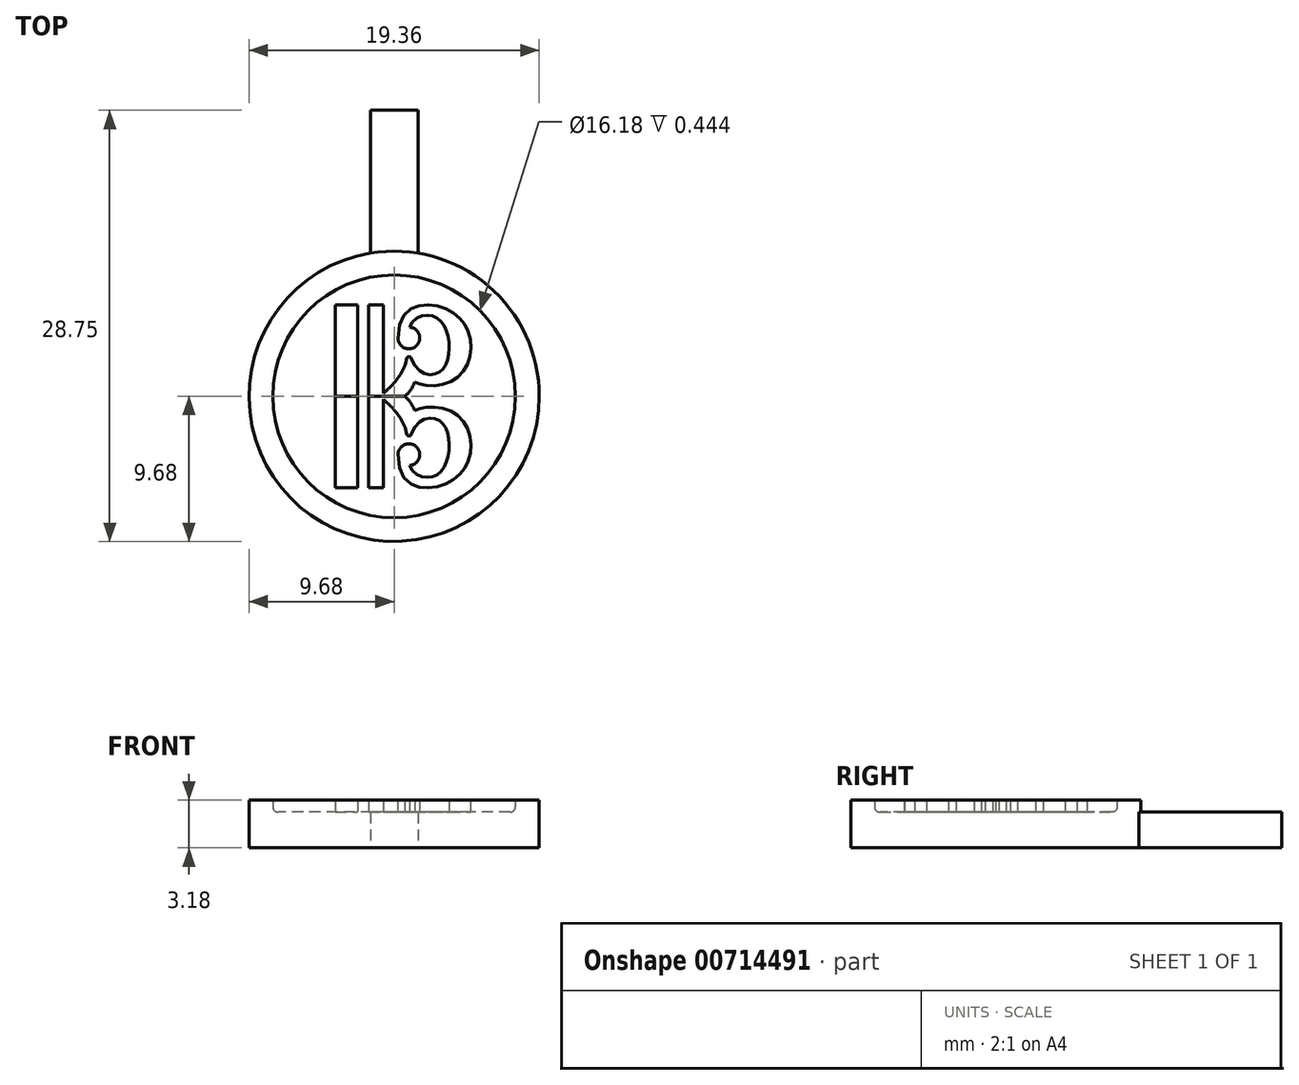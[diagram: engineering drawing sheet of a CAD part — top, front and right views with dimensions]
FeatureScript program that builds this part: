
annotation { "Feature Type Name" : "Feature", "Feature Type Description" : "" }
export const myFeature = defineFeature(function(context is Context, id is Id, definition is map)
    precondition{}
    {
        {
            var Q0;
            Q0=qCreatedBy(makeId("Top.planeOp"),FACE);
            var sketch = newSketch(context, id + "F0", { "sketchPlane" : qUnion([Q0])});
            skCircle(sketch, "E0", {"center": v(0, 0) * mm, "radius": 9.68 * mm});
            skSolve(sketch);
        }
        {
            var Q0;
            Q0 = qSketchRegion(id + "F0", true);
            extrude(context, id + "F1", {"entities" : qUnion([Q0]), "depth" : 2.38 * mm, "offsetDistance" : 25.4 * mm});
        }
        {
            var Q0;
            Q0=makeQuery(id+"F1.opExtrude","CAP_FACE",FACE,{"disambiguationData":[OSD([sQuery(id+"F0.wireOp",EDGE,"E0")])],"isStart":false});
            var sketch = newSketch(context, id + "F2", { "sketchPlane" : qUnion([Q0])});
            skCircle(sketch, "E1.0.0", {"center": v(0, 0) * mm, "radius": 9.68 * mm});
            skCircle(sketch, "E2.0", {"center": v(0, 0) * mm, "radius": 8.09 * mm});
            skSolve(sketch);
        }
        {
            var Q0;
            Q0=makeQuery(id+"F2.imprint","IMPRINT",FACE,{"disambiguationData":[TD([[makeQuery(id+"F2.imprint","IMPRINT",EDGE,{"derivedFrom":sQuery(id+"F2.wireOp",EDGE,"E1.0.0")}),1.0]])]});
            extrude(context, id + "F3", {"entities" : qUnion([Q0]), "operationType" : NewBodyOperationType.ADD, "depth" : 0.8 * mm, "offsetDistance" : 25.4 * mm});
        }
        {
            var Q0;
            Q0=qCreatedBy(makeId("Top.planeOp"),FACE);
            var sketch = newSketch(context, id + "F4", { "sketchPlane" : qUnion([Q0])});
            skLineSegment(sketch, "E3.bottom", {"start": v(1.59, 9.55) * mm, "end": v(-1.59, 9.55) * mm});
            skLineSegment(sketch, "E3.top", {"start": v(1.59, 19.07) * mm, "end": v(-1.59, 19.07) * mm});
            skLineSegment(sketch, "E3.left", {"start": v(1.59, 9.55) * mm, "end": v(1.59, 19.07) * mm});
            skLineSegment(sketch, "E3.right", {"start": v(-1.59, 9.55) * mm, "end": v(-1.59, 19.07) * mm});
            skPoint(sketch, "E3.middle", {"position": v(0, 14.3) * mm});
            skSolve(sketch);
        }
        {
            var Q0;
            Q0 = qSketchRegion(id + "F4", true);
            var Q1;
            Q1=makeQuery(id+"F3.opExtrude","CAP_FACE",FACE,{"disambiguationData":[OSD([sQuery(id+"F2.wireOp",EDGE,"E1.0.0"),sQuery(id+"F2.wireOp",EDGE,"E2.0")])],"isStart":false});
            extrude(context, id + "F5", {"entities" : qUnion([Q0]), "operationType" : NewBodyOperationType.ADD, "depth" : 2.38 * mm, "endBoundEntityFace" : qUnion([Q1]), "hasOffset" : true, "offsetDistance" : 1 * mm});
        }
        {
            var Q0;
            Q0=makeQuery(id+"F1.opExtrude","CAP_FACE",FACE,{"disambiguationData":[OSD([sQuery(id+"F0.wireOp",EDGE,"E0")])],"isStart":false});
            var sketch = newSketch(context, id + "F6", { "sketchPlane" : qUnion([Q0])});
            skLineSegment(sketch, "E4", {"start": v(0, 0) * mm, "end": v(12.28, 0) * mm, "construction": true});
            skLineSegment(sketch, "E5.bottom", {"start": v(-1.7, 6.09) * mm, "end": v(-0.73, 6.09) * mm});
            skLineSegment(sketch, "E5.top", {"start": v(-1.7, 0) * mm, "end": v(-0.73, 0) * mm});
            skLineSegment(sketch, "E5.left", {"start": v(-1.7, 6.09) * mm, "end": v(-1.7, 0) * mm});
            skLineSegment(sketch, "E5.right", {"start": v(-0.73, 6.09) * mm, "end": v(-0.73, 0) * mm});
            skLineSegment(sketch, "E6.bottom", {"start": v(-3.9, 6.09) * mm, "end": v(-2.44, 6.09) * mm});
            skLineSegment(sketch, "E6.top", {"start": v(-3.9, 0) * mm, "end": v(-2.44, 0) * mm});
            skLineSegment(sketch, "E6.left", {"start": v(-3.9, 6.09) * mm, "end": v(-3.9, 0) * mm});
            skLineSegment(sketch, "E6.right", {"start": v(-2.44, 6.09) * mm, "end": v(-2.44, 0) * mm});
            skCircle(sketch, "E7", {"center": v(0.99, 3.89) * mm, "radius": 0.72 * mm});
            skCircle(sketch, "E8", {"center": v(1, 2.5) * mm, "radius": 0.15 * mm});
            skLineSegment(sketch, "E9", {"start": v(-0.73, 0) * mm, "end": v(0.7, 0) * mm});
            skFitSpline(sketch, "E10", {"points": [v(-0.73, 0.2) * mm, v(0.85, 2.53) * mm], "startDerivative": vector(1.03, 0.78) * mm, "endDerivative": vector(0.54, 3.26) * mm});
            skFitSpline(sketch, "E11", {"points": [v(1.14, 2.55) * mm, v(3, 1.6) * mm, v(3.67, 3.44) * mm, v(2.73, 5.3) * mm, v(1.03, 4.6) * mm], "startDerivative": vector(4.65, -13.32) * mm, "endDerivative": vector(-3.35, -9.47) * mm});
            skFitSpline(sketch, "E12", {"points": [v(0.7, 0) * mm, v(1.38, 0.97) * mm], "startDerivative": vector(0.86, 0.64) * mm, "endDerivative": vector(0.38, 1) * mm});
            skFitSpline(sketch, "E13", {"points": [v(1.38, 0.97) * mm, v(3.93, 1.06) * mm, v(5.08, 3.81) * mm, v(3, 6) * mm, v(0.27, 3.87) * mm], "startDerivative": vector(5.04, -4.13) * mm, "endDerivative": vector(0.52, -23.86) * mm});
            skSolve(sketch);
        }
        {
            var Q0;
            Q0 = qSketchRegion(id + "F6", true);
            var Q1;
            Q1=makeQuery(id+"F3.opExtrude","CAP_FACE",FACE,{"disambiguationData":[OSD([sQuery(id+"F2.wireOp",EDGE,"E1.0.0"),sQuery(id+"F2.wireOp",EDGE,"E2.0")])],"isStart":false});
            extrude(context, id + "F7", {"entities" : qUnion([Q0]), "endBound" : BoundingType.UP_TO_SURFACE, "depth" : 25 * mm, "endBoundEntityFace" : qUnion([Q1]), "offsetDistance" : 25 * mm});
        }
        {
            var Q0;
            Q0=makeQuery(id+"F7.opExtrude","SWEPT_BODY",BODY,{"disambiguationData":[OSD([sQuery(id+"F6.wireOp",EDGE,"E6.bottom"),sQuery(id+"F6.wireOp",EDGE,"E6.top"),sQuery(id+"F6.wireOp",EDGE,"E6.left"),sQuery(id+"F6.wireOp",EDGE,"E6.right")])]});
            var Q1;
            Q1=makeQuery(id+"F7.opExtrude","SWEPT_BODY",BODY,{"disambiguationData":[OSD([sQuery(id+"F6.wireOp",EDGE,"E5.bottom"),sQuery(id+"F6.wireOp",EDGE,"E5.top"),sQuery(id+"F6.wireOp",EDGE,"E5.left"),sQuery(id+"F6.wireOp",EDGE,"E5.right"),sQuery(id+"F6.wireOp",EDGE,"E7"),sQuery(id+"F6.wireOp",EDGE,"E8"),sQuery(id+"F6.wireOp",EDGE,"E9"),sQuery(id+"F6.wireOp",EDGE,"E10"),sQuery(id+"F6.wireOp",EDGE,"E11"),sQuery(id+"F6.wireOp",EDGE,"E12"),sQuery(id+"F6.wireOp",EDGE,"E13")])]});
            var Q2;
            Q2=makeQuery(id+"F7.opExtrude","SWEPT_FACE",FACE,{"disambiguationData":[OSD([sQuery(id+"F6.wireOp",EDGE,"E5.top"),sQuery(id+"F6.wireOp",EDGE,"E9")])]});
            mirror(context, id + "F8", {"entities" : qUnion([Q0, Q1]), "mirrorPlane" : qUnion([Q2])});
        }
        {
            var Q0;
            Q0=makeQuery(id+"F1.opExtrude","CAP_FACE",FACE,{"disambiguationData":[OSD([sQuery(id+"F0.wireOp",EDGE,"E0")])],"isStart":false});
            fillet(context, id + "F9", {"entities" : qUnion([Q0]), "radius" : .35 * mm, "tangentPropagation" : true, "allowEdgeOverflow" : false});
        }
    });
